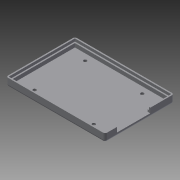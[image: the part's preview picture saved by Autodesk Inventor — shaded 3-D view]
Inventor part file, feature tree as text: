
AUTODESK INVENTOR PART (.ipt)
format: ipt  version: 2015 (Build 190159000, 159)  size: 155,136 bytes
history: native  units: in
note: dims shown in document units (in); Inventor stores cm internally (conversion verified against a paired STEP export)
features: sketch x5, extrude x4, fillet x1, hole x1
ambient origin geometry x8: Origin, YZ Plane, XZ Plane, XY Plane, X Axis, Y Axis, Z Axis, Center Point
bodies: Solid1 (feature_tree)
feature tree (11):
  extrude  "Extrusion1"  Depth=3.622in
  extrude  "Extrusion2"  Depth=0.0984in
  fillet  "Fillet1"  Radius=0.0984in
  extrude  "Extrusion3"  Depth=0.0984in
  hole  "Hole1"  [1 undecoded]
  extrude  "Extrusion4"  Depth=0.0492in
  sketch  "Sketch1"  dims[d0=2.5197in d1=3.622in]
  sketch  "Sketch2"  dims[d2=0.2953in d3=0.0in d4=0.0984in d5=0.0984in]
  sketch  "Sketch3"  dims[d6=0.0984in d7=0.0984in]
  sketch  "Sketch4"  dims[d8=0.2362in d9=0.0in d10=0.0787in]
  sketch  "Sketch5"  dims[d11=0.0492in d12=0.0492in d13=0.0492in d14=0.0492in d15=0.0984in d16=0.0in d17=0.0984in d18=0.0984in d19=0.0984in d20=0.0984in d21=0.5512in d22=0.5118in d23=2.126in d24=3.2283in d25=0.1378in d26=0.1378in d27=0.1181in d28=0.2362in d29=0.1575in d30=0.0787in d31=90.0deg d32=0.315in d33=0.8108in d34=0.0in d35=0.3543in d36=0.7874in d37=0.1772in d38=0.0984in d39=0.0in d41=0.2165in d42=0.0394in d43=0.0591in d44=0.6299in d45=0.7283in d46=0.6496in]
note: 1 required parameter value undecoded (feature->parameter linkage not recoverable at this tier; creation-order binding heuristic only, values carry confidence <= 0.55)
